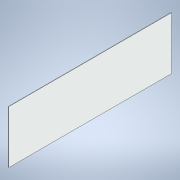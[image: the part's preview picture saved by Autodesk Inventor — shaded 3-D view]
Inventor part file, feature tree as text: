
AUTODESK INVENTOR PART (.ipt)
format: ipt  version: 2022 (Build 260153000, 153)  size: 97,280 bytes
history: native  units: mm
features: extrude x1, sketch x1
ambient origin geometry x8: Origin, YZ Plane, XZ Plane, XY Plane, X Axis, Y Axis, Z Axis, Center Point
bodies: Solid1 (feature_tree)
feature tree (2):
  extrude  "Extrusion1"  Depth=1118.0mm
  sketch  "Sketch1"  dims[d0=363.0mm d1=1118.0mm d2=3.0mm d3=0.0mm]
